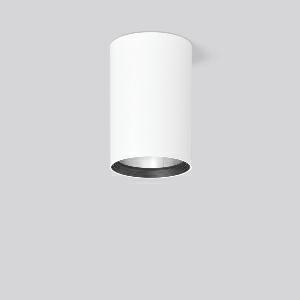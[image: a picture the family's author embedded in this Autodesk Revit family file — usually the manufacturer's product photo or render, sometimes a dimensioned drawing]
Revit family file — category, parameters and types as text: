
# Revit family: heledon_maxi_a_931225_002_1_5653
name_source: partatom
category: Lighting Fixtures
units: mm (PartAtom-declared; Revit-internal decimal feet)

## family parameters
Cut with Voids When Loaded = No
Host = Face
Light Source = No
Part Type = Normal
Room Calculation Point = No
Round Connector Dimension = Use Diameter
Shared = No

## types (1)
- HELEDON maxi A (1 x LED Modul 940, 4550 lm, 4000)
    Apparent Load = 35 VA
    Approval mark = CE
    CIE Flux Codes = 100 100 100 100 100
    Color Rendering = 92
    Color Temperature = 4000
    Default Elevation = 1800 mm
    Description = Series: HELEDON maxi
Cylindrical surface-mounted downlight. Housing: die-cast aluminium, powder-coated. Internal ceiling frame polycarbonate with bayonet mounting. Black plastic ring and recessed LED to prevent glare from the side. Optical assembly with reflector made of MIRO-Silver with 98% total light reflection for outstanding efficiency - can be changed without tools. Best colour rendering index Ra>90. Suitable for Ceiling mounting. Easy installation with a separate ceiling frame with bayonet mounting and plug connection. Driver integrated. Connected via plug-in connector. High quality converter without flickering and stroboscopic effect. The following accessories can be mounted without use of tools: interchangeable lenses, decorative glasses, honeycomb louvre, clear and frosted diffusers, white interchangeable plastic ring. 
Colour: traffic white, matt (RAL 9016)
Diameter: 123 mm
Height: 183 mm
Lamp: LED
Socket: without socket
Colour temperature: 4000K
Colour rendering index (CRI): 92
System power: 35 W
Rated luminous flux: 4550 lm
Luminous efficiency: 130 lm/W
Control gear: Regulated power supply
Protection class: I
Type of protection: IP 20
    Height = 183 mm
    Lamp = 1 x LED Modul 940
    Lamp Light Flux = 4550 lm
    Lamp count = 1
    Length = 123 mm
    Lifetime = 50000 h
    Luminous efficacy = 130 lm/W
    Manufacturer = RZB
    ModVariant = No
    Model = 931225.002.1
    Mounting Place = Ceiling
    Mounting Type = Surface mounted
    Number of Poles = 1
    OnlyDefault = Yes
    Power Factor = 1
    Product Name = HELEDON maxi A
    Product group = Surface mounted downlights
    ProductGroupID = 302
    Protection Class = Protection class I
    Protection Degree = IP 20
    RLX_Detail_Level = 1
    RLX_Emergency_Light_Flux = 0 lm
    RLX_Emergency_Type = 0
    RLX_Emergency_Type_DB = No
    RlxData = <blob elided: 97849 chars, md5=e2b49035>
    Socket = socket
    Standby Power = 0 W
    System Light Flux = 4550 lm
    System Power = 35 W
    Type Comments = Product without accessories
    Type Image = 931192.002.jpg
    URL = http://relux.com
    VarID = ---
    Voltage = 230 V
    Voltage Range = 220-240 V
    Weight = 0.00 kg
    Width = 0 mm  [stored 0 ft]

note: [stored X ft] marks values corroborated as IEEE doubles in the binary element streams (Revit-internal decimal feet)

## geometry (parser evidence)
native form markers: Blend x4, Sweep x9
no freeform markers — native parametric forms only
